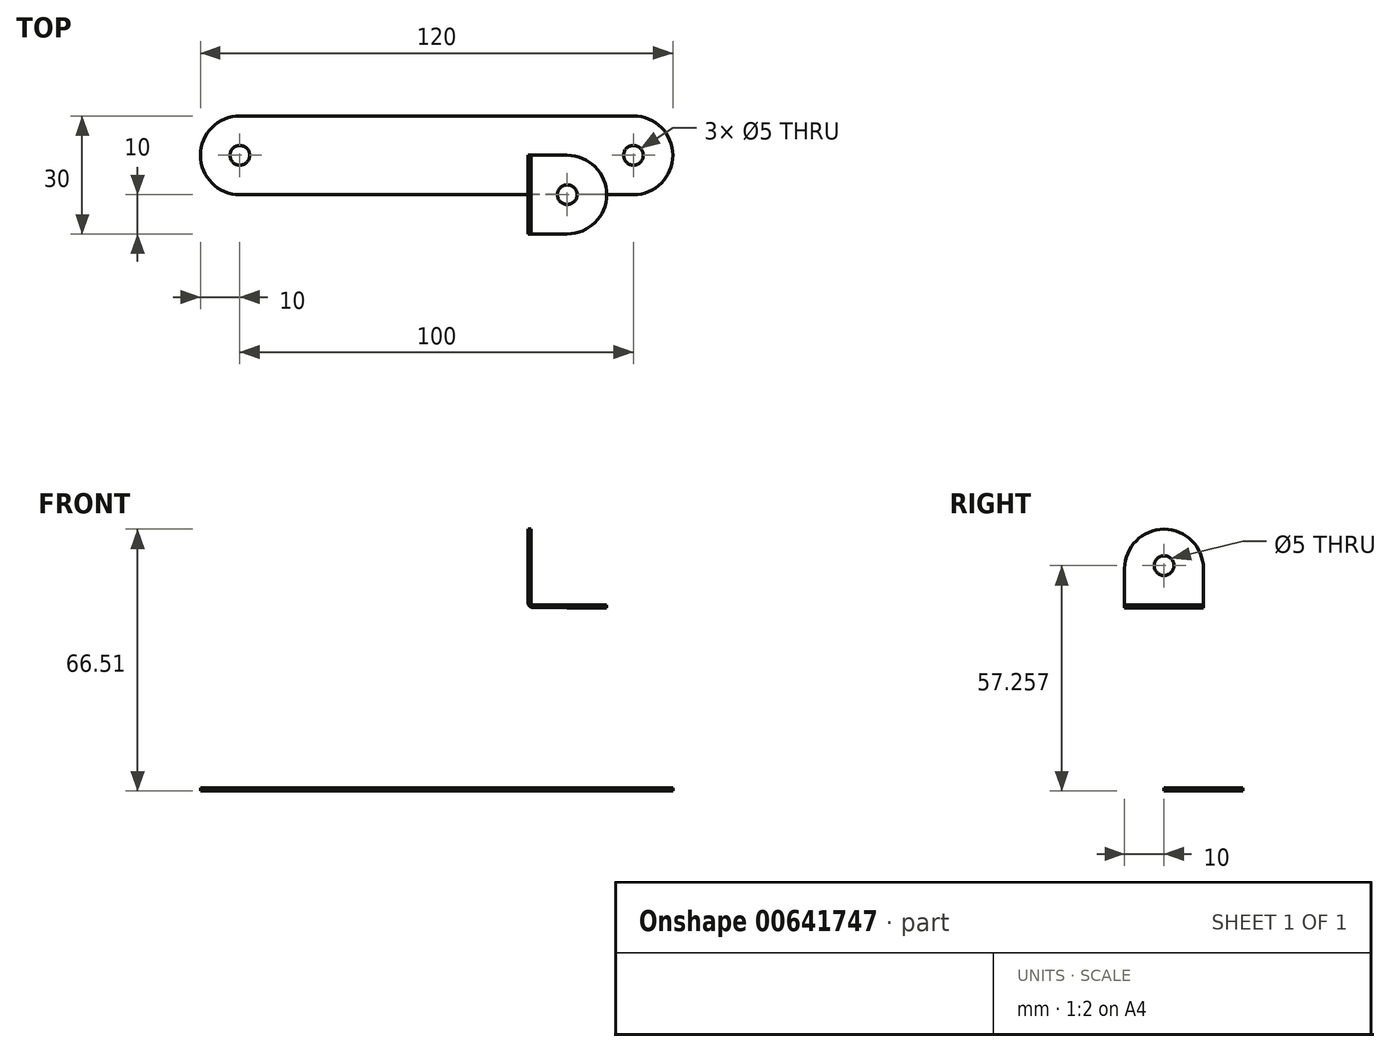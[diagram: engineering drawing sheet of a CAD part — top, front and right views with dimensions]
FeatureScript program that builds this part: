
annotation { "Feature Type Name" : "Feature", "Feature Type Description" : "" }
export const myFeature = defineFeature(function(context is Context, id is Id, definition is map)
    precondition{}
    {
        {
            var Q0;
            Q0=qCreatedBy(makeId("Top.planeOp"),FACE);
            var sketch = newSketch(context, id + "F0", { "sketchPlane" : qUnion([Q0])});
            skLineSegment(sketch, "E0.bottom", {"start": v(50, 10) * mm, "end": v(-50, 10) * mm});
            skLineSegment(sketch, "E0.top", {"start": v(50, -10) * mm, "end": v(-50, -10) * mm});
            skPoint(sketch, "E0.middle", {"position": v(0, 0) * mm});
            skArc(sketch, "E1", {"start": v(-50, 10) * mm, "mid": v(-60, 0) * mm, "end": v(-50, -10) * mm});
            skCircle(sketch, "E2", {"center": v(-50, 0) * mm, "radius": 2.5 * mm});
            skArc(sketch, "E3", {"start": v(50, -10) * mm, "mid": v(60, 0) * mm, "end": v(50, 10) * mm});
            skCircle(sketch, "E4.MirrorC", {"center": v(50, 0) * mm, "radius": 2.5 * mm});
            skSolve(sketch);
        }
        {
            var Q0;
            Q0=makeQuery(id+"F0.imprint","IMPRINT",FACE,{"disambiguationData":[TD([[makeQuery(id+"F0.imprint","IMPRINT",EDGE,{"derivedFrom":sQuery(id+"F0.wireOp",EDGE,"E0.bottom")}),1.0]])]});
            extrude(context, id + "F1", {"entities" : qUnion([Q0]), "depth" : 0.75 * mm, "offsetDistance" : 25 * mm});
        }
        {
            var Q0;
            Q0=qCreatedBy(makeId("Front.planeOp"),FACE);
            var sketch = newSketch(context, id + "F2", { "sketchPlane" : qUnion([Q0])});
            skLineSegment(sketch, "E5.0", {"start": v(24.68, 47.26) * mm, "end": v(43.18, 47.26) * mm});
            skLineSegment(sketch, "E5.1", {"start": v(23.93, 66.5) * mm, "end": v(23.93, 48) * mm});
            skLineSegment(sketch, "E6", {"start": v(23.18, 66.5) * mm, "end": v(23.93, 66.5) * mm});
            skLineSegment(sketch, "E7", {"start": v(43.18, 47.26) * mm, "end": v(43.18, 46.5) * mm});
            skPoint(sketch, "E8.visualSharp", {"position": v(23.93, 47.26) * mm});
            skLineSegment(sketch, "E9.filletArc", {"start": v(23.93, 47.26) * mm, "end": v(23.93, 47.26) * mm});
            skArc(sketch, "E10.filletArc", {"start": v(23.93, 48) * mm, "mid": v(24.15, 47.48) * mm, "end": v(24.68, 47.26) * mm});
            skArc(sketch, "E11.0", {"start": v(23.18, 48) * mm, "mid": v(23.46, 47.14) * mm, "end": v(24.18, 46.6) * mm});
            skLineSegment(sketch, "E12", {"start": v(43.18, 46.5) * mm, "end": v(24.18, 46.6) * mm});
            skLineSegment(sketch, "E13", {"start": v(23.18, 66.5) * mm, "end": v(23.18, 48) * mm});
            skSolve(sketch);
        }
        {
            var Q0;
            Q0 = qSketchRegion(id + "F2", true);
            extrude(context, id + "F3", {"entities" : qUnion([Q0]), "depth" : 20 * mm, "offsetDistance" : 25 * mm});
        }
        {
            var Q0;
            Q0=makeQuery(id+"F3.opExtrude","SWEPT_FACE",FACE,{"disambiguationData":[OSD([sQuery(id+"F2.wireOp",EDGE,"E5.0")])]});
            var sketch = newSketch(context, id + "F4", { "sketchPlane" : qUnion([Q0])});
            skCircle(sketch, "E14", {"center": v(33.18, -10) * mm, "radius": 2.5 * mm});
            skPoint(sketch, "E14.centerSnap0", {"position": v(43.18, -10) * mm});
            skSolve(sketch);
        }
        {
            var Q0;
            Q0=sQuery(id+"F4.wireOp",VERTEX,"E14.center");
            var Q1;
            Q1=makeQuery(id+"F1.opExtrude","SWEPT_BODY",BODY,{"disambiguationData":[OSD([sQuery(id+"F0.wireOp",EDGE,"E0.bottom"),sQuery(id+"F0.wireOp",EDGE,"E0.top"),sQuery(id+"F0.wireOp",EDGE,"E1"),sQuery(id+"F0.wireOp",EDGE,"E2"),sQuery(id+"F0.wireOp",EDGE,"E3"),sQuery(id+"F0.wireOp",EDGE,"E4.MirrorC")])]});
            var Q2;
            Q2=makeQuery(id+"F3.opExtrude","SWEPT_BODY",BODY,{"disambiguationData":[OSD([sQuery(id+"F2.wireOp",EDGE,"E5.0"),sQuery(id+"F2.wireOp",EDGE,"E5.1"),sQuery(id+"F2.wireOp",EDGE,"E6"),sQuery(id+"F2.wireOp",EDGE,"E7"),sQuery(id+"F2.wireOp",EDGE,"E10.filletArc"),sQuery(id+"F2.wireOp",EDGE,"E11.0"),sQuery(id+"F2.wireOp",EDGE,"E12"),sQuery(id+"F2.wireOp",EDGE,"E13")])]});
            hole(context, id + "F5", {"style" : HoleStyle.SIMPLE, "endStyle" : HoleEndStyle.THROUGH, "holeDiameter" : 5 * mm, "majorDiameter" : 5 * mm, "isTappedThrough" : true, "tappedDepth" : 12 * mm, "tapClearance" : 3, "locations" : qUnion([Q0]), "scope" : qUnion([Q1, Q2])});
        }
        {
            var Q0;
            Q0=makeQuery(id+"F3.opExtrude","SWEPT_FACE",FACE,{"disambiguationData":[OSD([sQuery(id+"F2.wireOp",EDGE,"E5.1")])]});
            var sketch = newSketch(context, id + "F6", { "sketchPlane" : qUnion([Q0])});
            skCircle(sketch, "E15", {"center": v(-10, 57.26) * mm, "radius": 2.5 * mm});
            skPoint(sketch, "E15.centerSnap0", {"position": v(-20, 57.26) * mm});
            skSolve(sketch);
        }
        {
            var Q0;
            Q0=sQuery(id+"F6.wireOp",VERTEX,"E15.center");
            var Q1;
            Q1=makeQuery(id+"F3.opExtrude","SWEPT_BODY",BODY,{"disambiguationData":[OSD([sQuery(id+"F2.wireOp",EDGE,"E5.0"),sQuery(id+"F2.wireOp",EDGE,"E5.1"),sQuery(id+"F2.wireOp",EDGE,"E6"),sQuery(id+"F2.wireOp",EDGE,"E7"),sQuery(id+"F2.wireOp",EDGE,"E10.filletArc"),sQuery(id+"F2.wireOp",EDGE,"E11.0"),sQuery(id+"F2.wireOp",EDGE,"E12"),sQuery(id+"F2.wireOp",EDGE,"E13")])]});
            hole(context, id + "F7", {"style" : HoleStyle.SIMPLE, "endStyle" : HoleEndStyle.THROUGH, "holeDiameter" : 5 * mm, "majorDiameter" : 5 * mm, "isTappedThrough" : true, "tappedDepth" : 12 * mm, "tapClearance" : 3, "locations" : qUnion([Q0]), "scope" : qUnion([Q1])});
        }
        {
            var Q0;
            Q0=makeQuery(id+"F3.opExtrude","CAP_EDGE",EDGE,{"disambiguationData":[OSD([sQuery(id+"F2.wireOp",EDGE,"E6")])],"isStart":false});
            var Q1;
            Q1=makeQuery(id+"F3.opExtrude","CAP_EDGE",EDGE,{"disambiguationData":[OSD([sQuery(id+"F2.wireOp",EDGE,"E6")])],"isStart":true});
            var Q2;
            Q2=makeQuery(id+"F3.opExtrude","CAP_EDGE",EDGE,{"disambiguationData":[OSD([sQuery(id+"F2.wireOp",EDGE,"E7")])],"isStart":false});
            var Q3;
            Q3=makeQuery(id+"F3.opExtrude","CAP_EDGE",EDGE,{"disambiguationData":[OSD([sQuery(id+"F2.wireOp",EDGE,"E7")])],"isStart":true});
            fillet(context, id + "F8", {"entities" : qUnion([Q0, Q1, Q2, Q3]), "radius" : 10 * mm, "tangentPropagation" : true, "allowEdgeOverflow" : false});
        }
    });
